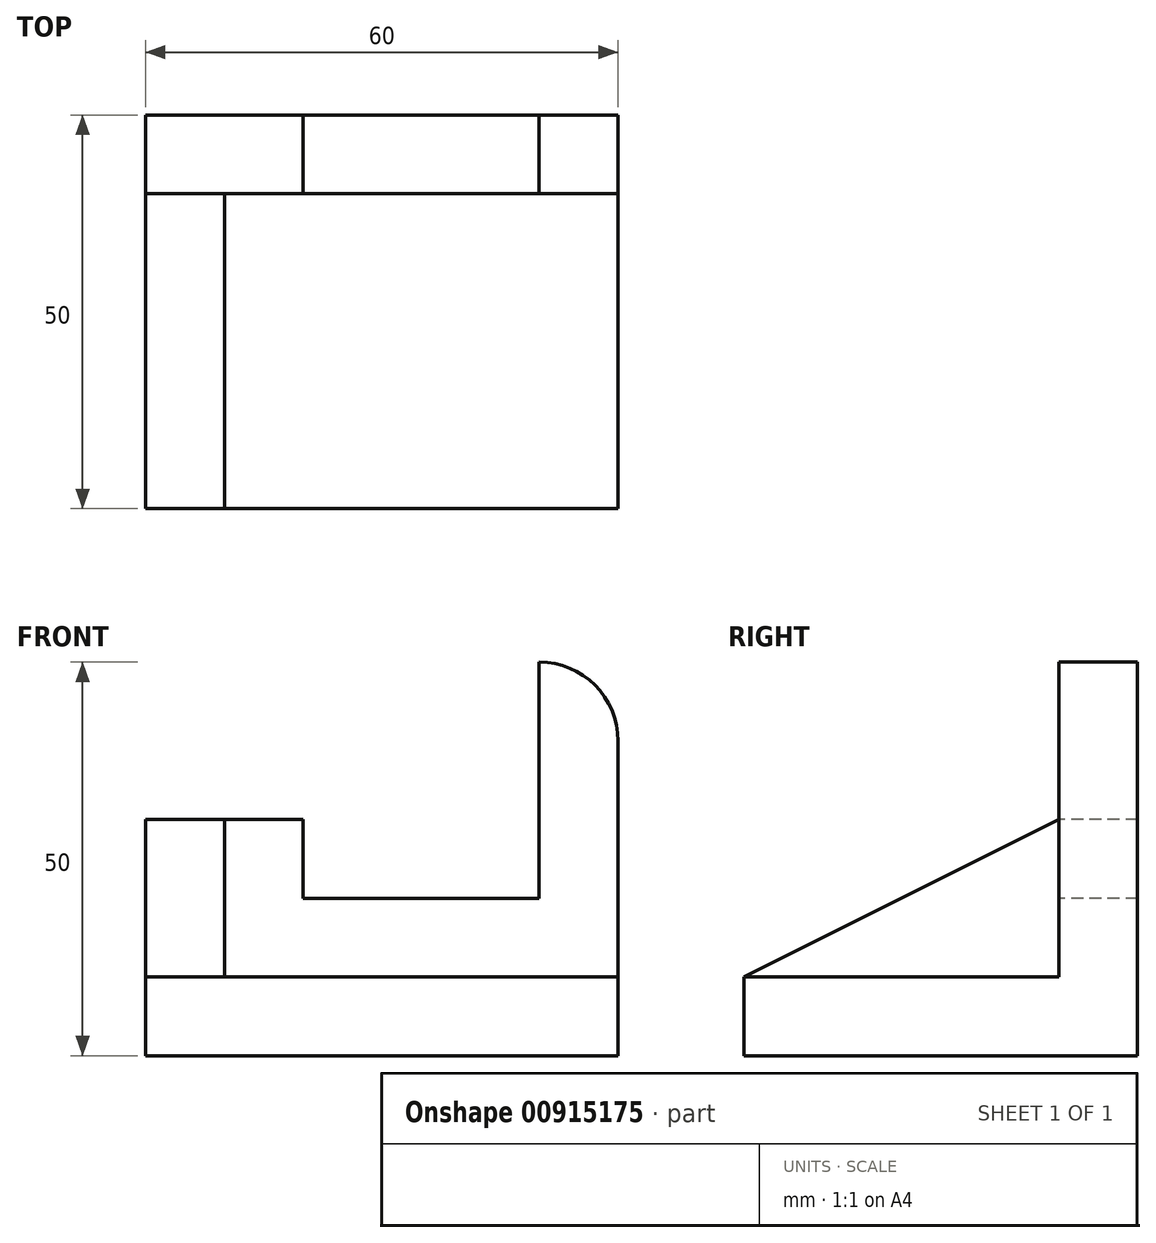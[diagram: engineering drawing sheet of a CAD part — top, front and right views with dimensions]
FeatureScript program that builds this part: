
annotation { "Feature Type Name" : "Feature", "Feature Type Description" : "" }
export const myFeature = defineFeature(function(context is Context, id is Id, definition is map)
    precondition{}
    {
        {
            var Q0;
            Q0=qCreatedBy(makeId("Top.planeOp"),FACE);
            var sketch = newSketch(context, id + "F0", { "sketchPlane" : qUnion([Q0])});
            skLineSegment(sketch, "E0.bottom", {"start": v(0, 0) * mm, "end": v(60, 0) * mm});
            skLineSegment(sketch, "E0.top", {"start": v(0, 50) * mm, "end": v(60, 50) * mm});
            skLineSegment(sketch, "E0.left", {"start": v(0, 0) * mm, "end": v(0, 50) * mm});
            skLineSegment(sketch, "E0.right", {"start": v(60, 0) * mm, "end": v(60, 50) * mm});
            skSolve(sketch);
        }
        {
            var Q0;
            Q0=makeQuery(id+"F0.imprint","IMPRINT",FACE,{"disambiguationData":[TD([[makeQuery(id+"F0.imprint","IMPRINT",EDGE,{"derivedFrom":sQuery(id+"F0.wireOp",EDGE,"E0.bottom")}),1.0]])]});
            extrude(context, id + "F1", {"entities" : qUnion([Q0]), "depth" : 10 * mm, "offsetDistance" : 25 * mm});
        }
        {
            var Q0;
            Q0=makeQuery(id+"F1.opExtrude","CAP_FACE",FACE,{"disambiguationData":[OSD([sQuery(id+"F0.wireOp",EDGE,"E0.bottom"),sQuery(id+"F0.wireOp",EDGE,"E0.top"),sQuery(id+"F0.wireOp",EDGE,"E0.left"),sQuery(id+"F0.wireOp",EDGE,"E0.right")])],"isStart":false});
            var sketch = newSketch(context, id + "F2", { "sketchPlane" : qUnion([Q0])});
            skLineSegment(sketch, "E1", {"start": v(10, 0) * mm, "end": v(10, 40) * mm});
            skLineSegment(sketch, "E2", {"start": v(10, 40) * mm, "end": v(60, 40) * mm});
            skSolve(sketch);
        }
        {
            var Q0;
            {var subQ3=sQuery(id+"F2.wireOp",EDGE,"E1");Q0=makeQuery(id+"F2.imprint","IMPRINT",FACE,{"disambiguationData":[TD([[makeQuery(id+"F2.imprint","IMPRINT",EDGE,{"derivedFrom":subQ3}),1.0]])]});}
            extrude(context, id + "F3", {"entities" : qUnion([Q0]), "operationType" : NewBodyOperationType.ADD, "depth" : 40 * mm, "offsetDistance" : 25 * mm});
        }
        {
            var Q0;
            Q0=makeQuery(id+"F3.opExtrude","SWEPT_FACE",FACE,{"disambiguationData":[OSD([sQuery(id+"F2.wireOp",EDGE,"E1")])]});
            var sketch = newSketch(context, id + "F4", { "sketchPlane" : qUnion([Q0])});
            skLineSegment(sketch, "E3", {"start": v(40, 30) * mm, "end": v(0, 30) * mm, "construction": true});
            skLineSegment(sketch, "E4", {"start": v(40, 30) * mm, "end": v(0, 10) * mm});
            skSolve(sketch);
        }
        {
            var Q0;
            {var subQ0=sQuery(id+"F4.wireOp",EDGE,"E4");Q0=makeQuery(id+"F4.imprint","IMPRINT",FACE,{"disambiguationData":[TD([[makeQuery(id+"F4.imprint","IMPRINT",EDGE,{"derivedFrom":subQ0}),-1.0]])]});}
            extrude(context, id + "F5", {"entities" : qUnion([Q0]), "operationType" : NewBodyOperationType.REMOVE, "endBound" : BoundingType.THROUGH_ALL, "oppositeDirection" : true, "depth" : 25 * mm, "offsetDistance" : 25 * mm});
        }
        {
            var Q0;
            {var subQ0=sQuery(id+"F2.wireOp",EDGE,"E2");Q0=makeQuery(id+"F5.boolean.opBoolean","MERGE",FACE,{"derivedFrom":[makeQuery(id+"F3.opExtrude","SWEPT_FACE",FACE,{"disambiguationData":[OSD([subQ0])]})],"fromTools":[makeQuery(id+"F5.opExtrude","SWEPT_FACE",FACE,{"disambiguationData":[OSD([sQuery(id+"F2.wireOp",EDGE,"E1"),subQ0])]})]});}
            var sketch = newSketch(context, id + "F6", { "sketchPlane" : qUnion([Q0])});
            skLineSegment(sketch, "E5.0", {"start": v(0, 30) * mm, "end": v(10, 30) * mm});
            skLineSegment(sketch, "E6", {"start": v(10, 30) * mm, "end": v(20, 30) * mm});
            skLineSegment(sketch, "E7", {"start": v(20, 30) * mm, "end": v(20, 20) * mm});
            skLineSegment(sketch, "E8", {"start": v(20, 20) * mm, "end": v(50, 20) * mm});
            skLineSegment(sketch, "E9", {"start": v(50, 20) * mm, "end": v(50, 50) * mm});
            skLineSegment(sketch, "E10.0", {"start": v(0, 50) * mm, "end": v(50, 50) * mm});
            skLineSegment(sketch, "E11.0", {"start": v(60, 40) * mm, "end": v(60, 10) * mm});
            skPoint(sketch, "E12.visualSharp", {"position": v(60, 50) * mm});
            skArc(sketch, "E12.filletArc", {"start": v(60, 40) * mm, "mid": v(57.07, 47.07) * mm, "end": v(50, 50) * mm});
            skSolve(sketch);
        }
        {
            var Q0;
            {var subQ0=sQuery(id+"F6.wireOp",EDGE,"E12.filletArc");Q0=makeQuery(id+"F6.imprint","IMPRINT",FACE,{"disambiguationData":[TD([[makeQuery(id+"F6.imprint","IMPRINT",EDGE,{"derivedFrom":subQ0}),-1.0]])]});}
            var Q1;
            Q1=makeQuery(id+"F6.imprint","IMPRINT",FACE,{"disambiguationData":[TD([[makeQuery(id+"F6.imprint","IMPRINT",EDGE,{"derivedFrom":sQuery(id+"F6.wireOp",EDGE,"E5.0")}),1.0]])]});
            extrude(context, id + "F7", {"entities" : qUnion([Q0, Q1]), "operationType" : NewBodyOperationType.REMOVE, "endBound" : BoundingType.THROUGH_ALL, "oppositeDirection" : true, "depth" : 25 * mm, "offsetDistance" : 25 * mm});
        }
    });
